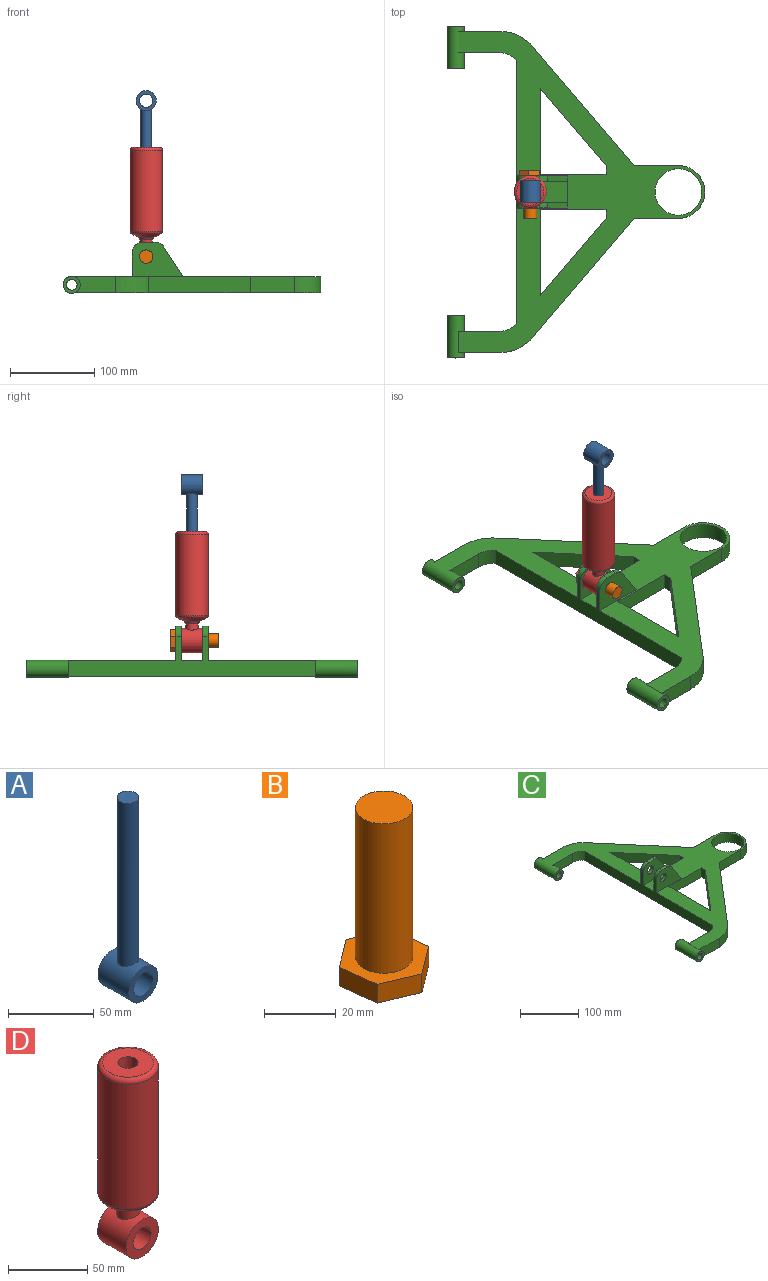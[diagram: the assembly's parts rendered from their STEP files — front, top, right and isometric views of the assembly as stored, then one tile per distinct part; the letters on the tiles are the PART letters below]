
ASSEMBLY  parts=4 mates=3
PART A: 6 faces, bbox 24x25.4x139 mm
  f0: cylinder r=11.98mm len=25.4mm, axis (0,1,0), area 1780.7mm2, adj f2,f3,f4
  f1: cylinder r=7.94mm len=25.4mm, axis (0,1,0), area 1266.8mm2, adj f2,f3
  f2: plane 23.96x23.96mm, normal (0,-1,0), area 253mm2, adj f0,f1
  f3: plane 23.96x23.96mm, normal (0,1,0), area 253mm2, adj f0,f1
  f4: cylinder r=6.35mm len=116.84mm, axis (0,0,-1), area 4624.7mm2, adj f0,f5
  f5: plane 12.7x12.7mm, normal (0,0,1), area 126.7mm2, adj f4
PART B: 10 faces, bbox 24.6x26.6x57.2 mm
  f0: plane 10.71x8.03mm, normal (0.6,-0.8,0), area 85mm2, adj f1,f5,f6,f7
  f1: plane 13.29x6.35mm, normal (0.99,0.12,0), area 85mm2, adj f0,f2,f6,f7
  f2: plane 12.31x6.35mm, normal (0.39,0.92,0), area 85mm2, adj f1,f3,f6,f7
  f3: plane 10.71x8.03mm, normal (-0.6,0.8,0), area 85mm2, adj f2,f4,f6,f7
  f4: plane 13.29x6.35mm, normal (-0.99,-0.12,0), area 85mm2, adj f3,f5,f6,f7
  f5: plane 12.31x6.35mm, normal (-0.39,-0.92,0), area 85mm2, adj f0,f4,f6,f7
  f6: plane 26.59x24.63mm, normal (0,0,-1), area 465.8mm2, adj f0,f1,f2,f3,f4,f5
  f7: plane 26.59x24.63mm, normal (0,0,1), area 267.8mm2, adj f0,f1,f2,f3,f4,f5,f8
  f8: cylinder r=7.94mm len=50.8mm, axis (0,0,-1), area 2533.5mm2, adj f7,f9
  f9: plane 15.88x15.88mm, normal (0,0,1), area 197.9mm2, adj f8
PART C: 52 faces, bbox 305.6x393.7x60.7 mm
  f0: plane 14.38x6.35mm, normal (0,0,1), area 91.3mm2, adj f2,f3,f48,f51
  f1: plane 35.27x22.84mm, normal (0.84,0,0.54), area 266.8mm2, adj f2,f35,f48,f51
  f2: cylinder r=12.7mm len=10.66mm, axis (0,1,0), area 80.3mm2, adj f0,f1,f48,f51
  f3: cylinder r=12.7mm len=12.7mm, axis (0,1,0), area 126.7mm2, adj f0,f18,f48,f51
  f4: cylinder r=7.94mm len=15.88mm, axis (0,1,0), area 316.7mm2, adj f48,f51
  f5: cylinder r=6.35mm len=50.8mm, axis (0,-1,0), area 2026.8mm2, adj f7,f8
  f6: cylinder r=10.13mm len=50.8mm, axis (0,-1,0), area 2601.9mm2, adj f7,f8,f20,f21,f22,f41
  f7: plane 20.25x20.25mm, normal (0,-1,0), area 195.4mm2, adj f5,f6
  f8: plane 20.25x20.25mm, normal (0,1,0), area 195.4mm2, adj f5,f6
  f9: plane 25.4x0mm, normal (-1,0,0), area 0mm2, adj f16,f30,f35,f39
  f10: plane 19.05x10.4mm, normal (-1,0,0), area 198.2mm2, adj f11,f31,f35,f36
  f11: plane 91.57x78.13mm, normal (-0.76,0.65,0), area 2293.1mm2, adj f10,f12,f35,f36
  f12: plane 101.97x19.05mm, normal (1,0,0), area 1942.5mm2, adj f11,f31,f35,f36
  f13: plane 101.97x19.05mm, normal (1,0,0), area 1942.5mm2, adj f14,f32,f35,f36
  f14: plane 91.57x78.13mm, normal (-0.76,-0.65,0), area 2293.1mm2, adj f13,f15,f35,f36
  f15: plane 19.05x10.4mm, normal (-1,0,0), area 198.2mm2, adj f14,f32,f35,f36
  f16: plane 48.95x19.05mm, normal (0,-1,0), area 839.6mm2, adj f9,f17,f33,f35,f36,f39
  f17: cylinder r=25.4mm len=19.32mm, axis (0,0,-1), area 418.3mm2, adj f16,f18,f35,f36
  f18: plane 312.37x47.42mm, normal (-1,0,0), area 6310.8mm2, adj f3,f17,f19,f35,f36,f45,f47,f48
  f19: cylinder r=25.4mm len=19.32mm, axis (0,0,-1), area 418.3mm2, adj f18,f20,f35,f36
  f20: plane 48.95x19.05mm, normal (0,1,0), area 839.6mm2, adj f6,f19,f21,f35,f36,f41
  f21: plane 25.4x0mm, normal (-1,0,0), area 0mm2, adj f6,f20,f22,f36
  f22: plane 48.95x19.05mm, normal (0,-1,0), area 839.6mm2, adj f6,f21,f23,f35,f36,f41
  f23: cylinder r=50.8mm len=38.64mm, axis (0,0,-1), area 836.5mm2, adj f22,f24,f35,f36
  f24: plane 141.36x120.62mm, normal (0.76,-0.65,0), area 3540.1mm2, adj f23,f25,f35,f36
  f25: plane 52.48x19.05mm, normal (0,-1,0), area 999.7mm2, adj f24,f26,f35,f36
  f26: cylinder r=31.31mm len=62.62mm, axis (0,0,-1), area 1873.8mm2, adj f25,f27,f35,f36
  f27: plane 52.48x19.05mm, normal (0,1,0), area 999.7mm2, adj f26,f28,f35,f36
  f28: plane 141.36x120.62mm, normal (0.76,0.65,0), area 3540.1mm2, adj f27,f29,f35,f36
  f29: cylinder r=50.8mm len=38.64mm, axis (0,0,-1), area 836.5mm2, adj f28,f30,f35,f36
  f30: plane 48.95x19.05mm, normal (0,1,0), area 839.6mm2, adj f9,f29,f33,f35,f36,f39
  f31: plane 78.13x19.05mm, normal (0,-1,0), area 1488.4mm2, adj f10,f12,f35,f36
  f32: plane 78.13x19.05mm, normal (0,1,0), area 1488.4mm2, adj f13,f15,f35,f36
  f33: plane 25.4x0mm, normal (-1,0,0), area 0mm2, adj f16,f30,f36,f39
  f34: cylinder r=27.62mm len=55.23mm, axis (0,0,-1), area 3305.6mm2, adj f35,f36
  f35: plane 381.01x292.01mm, normal (0,0,1), area 26460.7mm2, adj f1,f9,f10,f11,f12,f13,f14,f15
  f36: plane 381x292mm, normal (0,0,-1), area 28768.6mm2, adj f10,f11,f12,f13,f14,f15,f16,f17
  f37: plane 20.25x20.25mm, normal (0,-1,0), area 195.4mm2, adj f39,f40
  f38: plane 20.25x20.25mm, normal (0,1,0), area 195.4mm2, adj f39,f40
  f39: cylinder r=10.13mm len=50.8mm, axis (0,-1,0), area 2601.9mm2, adj f9,f16,f30,f33,f37,f38
  f40: cylinder r=6.35mm len=50.8mm, axis (0,-1,0), area 2026.8mm2, adj f37,f38
  f41: plane 25.4x0mm, normal (-1,0,0), area 0mm2, adj f6,f20,f22,f35
  f42: plane 35.27x22.84mm, normal (0.84,0,0.54), area 266.8mm2, adj f35,f43,f47,f50
  f43: cylinder r=12.7mm len=10.66mm, axis (0,1,0), area 80.3mm2, adj f42,f44,f47,f50
  f44: plane 14.38x6.35mm, normal (0,0,1), area 91.3mm2, adj f43,f45,f47,f50
  f45: cylinder r=12.7mm len=12.7mm, axis (0,1,0), area 126.7mm2, adj f18,f44,f47,f50
  f46: cylinder r=7.94mm len=15.88mm, axis (0,1,0), area 316.7mm2, adj f47,f50
  f47: plane 60.58x41.07mm, normal (0,-1,0), area 1701.7mm2, adj f18,f35,f42,f43,f44,f45,f46
  f48: plane 60.58x41.07mm, normal (0,1,0), area 1701.7mm2, adj f0,f1,f2,f3,f4,f18,f35
  f49: plane 60.59x25.41mm, normal (0,0,1), area 1538.6mm2, adj f18,f35,f50,f51
  f50: plane 60.58x41.07mm, normal (0,1,0), area 1701.9mm2, adj f18,f42,f43,f44,f45,f46,f49
  f51: plane 60.58x41.07mm, normal (0,-1,0), area 1701.9mm2, adj f0,f1,f2,f3,f4,f18,f49
PART D: 13 faces, bbox 41.5x41.5x144 mm
  f0: cylinder r=14.46mm len=28.92mm, axis (0,1,0), area 2132.1mm2, adj f2,f3,f4
  f1: cylinder r=7.94mm len=25.4mm, axis (0,1,0), area 1266.8mm2, adj f2,f3
  f2: plane 28.92x28.92mm, normal (0,-1,0), area 459mm2, adj f0,f1
  f3: plane 28.92x28.92mm, normal (0,1,0), area 459mm2, adj f0,f1
  f4: cylinder r=7.36mm len=14.72mm, axis (0,0,-1), area 289.3mm2, adj f0,f9
  f5: torus R=16.01mm, axis (0,0,-1), area 402.2mm2, adj f6,f10
  f6: cylinder r=19.19mm len=96.51mm, axis (0,0,-1), area 11634.9mm2, adj f5,f7
  f7: torus R=16.01mm, axis (0,0,-1), area 565.1mm2, adj f6,f8
  f8: plane 32.02x32.02mm, normal (0,0,1), area 678.7mm2, adj f7,f11
  f9: torus R=10.53mm, axis (0,0,-1), area 171.8mm2, adj f4,f10
  f10: cone r=9.05mm half-angle=62.1deg, axis (0,0,1), area 797.2mm2, adj f5,f9
  f11: cylinder r=6.35mm len=101.6mm, axis (0,0,1), area 4053.7mm2, adj f8,f12
  f12: plane 12.7x12.7mm, normal (0,0,1), area 126.7mm2, adj f11
PLACE A rot(axis=(0,1,0),180deg) t=(-236.85,144.13,328.58)mm
PLACE B rot(axis=(1,0,0),90deg) t=(-125.19,163.18,60.4)mm
PLACE C t=(-235.26,-52.72,80.43)mm
PLACE D t=(-173.77,144.13,113.85)mm
MATE slider A.f4 <-> D.f11  axis (0,0,1) through (-173.77,144.13,230.48)mm
MATE fastened B.f8 <-> C.f4  axis (0,-1,0) through (-173.77,163.18,113.85)mm
MATE revolute D.f0 <-> B.f8  axis (0,1,0) through (-173.77,156.83,113.85)mm
